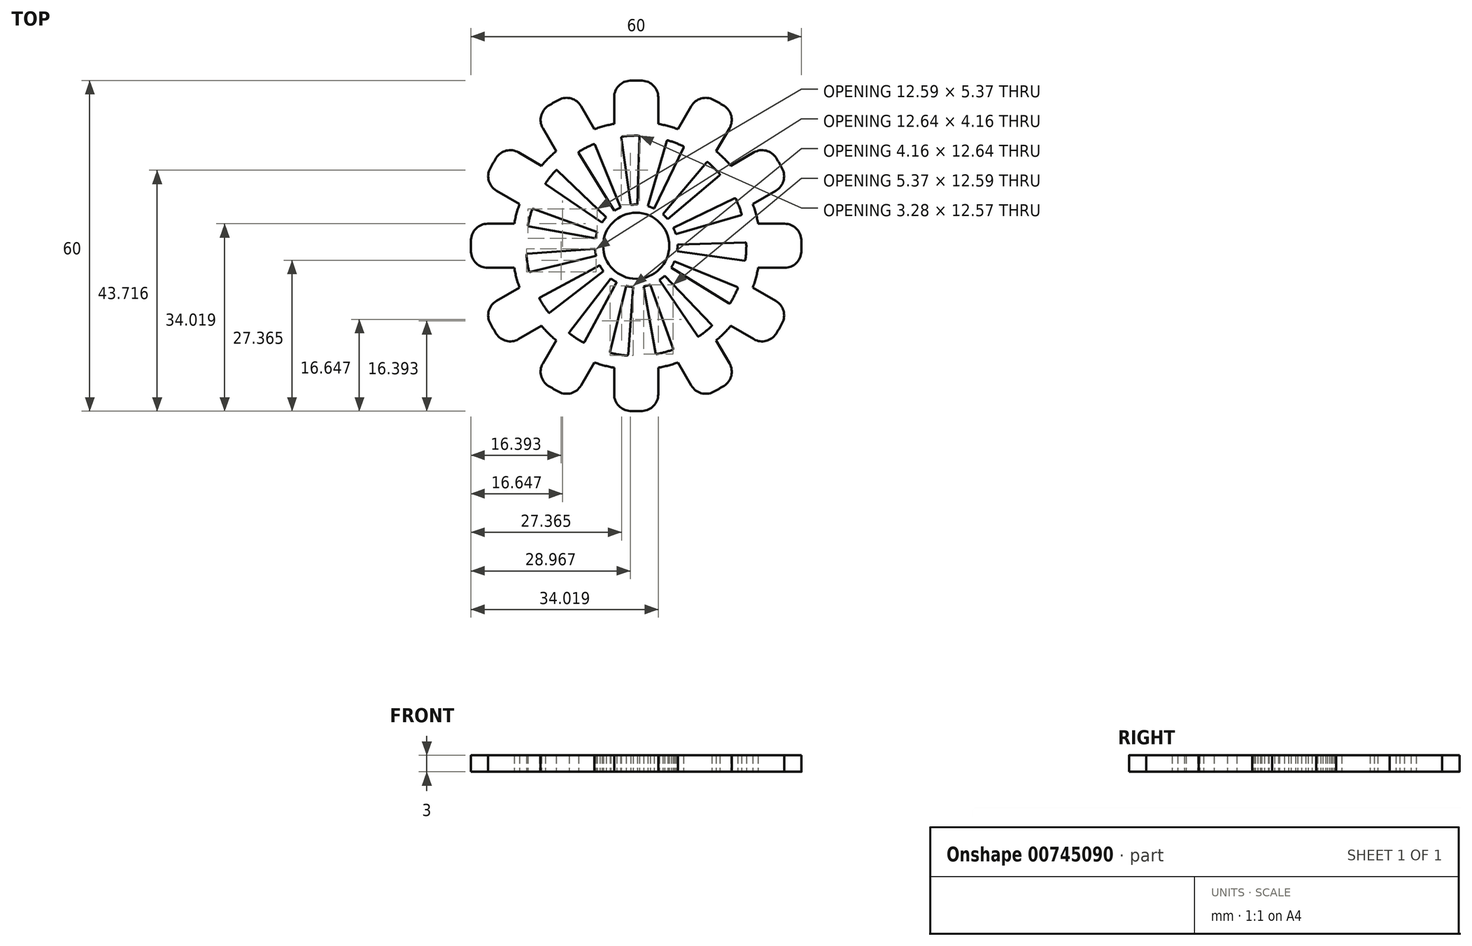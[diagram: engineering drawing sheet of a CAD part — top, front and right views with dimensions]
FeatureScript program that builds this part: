
annotation { "Feature Type Name" : "Feature", "Feature Type Description" : "" }
export const myFeature = defineFeature(function(context is Context, id is Id, definition is map)
    precondition{}
    {
        {
            var Q0;
            Q0=qCreatedBy(makeId("Top.planeOp"),FACE);
            var sketch = newSketch(context, id + "F0", { "sketchPlane" : qUnion([Q0])});
            skArc(sketch, "E0", {"start": v(-25.4, 15.95) * mm, "mid": v(-25.98, 15) * mm, "end": v(-26.52, 14.03) * mm});
            skArc(sketch, "E1", {"start": v(-7.06, 2.54) * mm, "mid": v(-7.24, 1.94) * mm, "end": v(-7.38, 1.33) * mm});
            skArc(sketch, "E2", {"start": v(-21.18, 7.6) * mm, "mid": v(-21.73, 5.82) * mm, "end": v(-22.14, 4) * mm});
            skLineSegment(sketch, "E3", {"start": v(-4, 22.14) * mm, "end": v(-4, 26.98) * mm});
            skLineSegment(sketch, "E4", {"start": v(4, 22.14) * mm, "end": v(4, 26.98) * mm});
            skLineSegment(sketch, "E5.1.0", {"start": v(-7.6, 21.18) * mm, "end": v(-10.03, 25.37) * mm});
            skLineSegment(sketch, "E5.1.1", {"start": v(-14.53, 17.18) * mm, "end": v(-16.95, 21.37) * mm});
            skLineSegment(sketch, "E5.2.0", {"start": v(-17.18, 14.53) * mm, "end": v(-21.37, 16.95) * mm});
            skLineSegment(sketch, "E5.2.1", {"start": v(-21.18, 7.6) * mm, "end": v(-25.37, 10.03) * mm});
            skLineSegment(sketch, "E5.3.0", {"start": v(-22.14, 4) * mm, "end": v(-26.98, 4) * mm});
            skLineSegment(sketch, "E5.3.1", {"start": v(-22.14, -4) * mm, "end": v(-26.98, -4) * mm});
            skLineSegment(sketch, "E5.4.0", {"start": v(-21.18, -7.6) * mm, "end": v(-25.37, -10.03) * mm});
            skLineSegment(sketch, "E5.4.1", {"start": v(-17.18, -14.53) * mm, "end": v(-21.37, -16.95) * mm});
            skLineSegment(sketch, "E5.5.0", {"start": v(-14.53, -17.18) * mm, "end": v(-16.95, -21.37) * mm});
            skLineSegment(sketch, "E5.5.1", {"start": v(-7.6, -21.18) * mm, "end": v(-10.03, -25.37) * mm});
            skLineSegment(sketch, "E5.6.0", {"start": v(-4, -22.14) * mm, "end": v(-4, -26.98) * mm});
            skLineSegment(sketch, "E5.6.1", {"start": v(4, -22.14) * mm, "end": v(4, -26.98) * mm});
            skLineSegment(sketch, "E5.7.0", {"start": v(7.6, -21.18) * mm, "end": v(10.03, -25.37) * mm});
            skLineSegment(sketch, "E5.7.1", {"start": v(14.53, -17.18) * mm, "end": v(16.95, -21.37) * mm});
            skLineSegment(sketch, "E5.8.0", {"start": v(17.18, -14.53) * mm, "end": v(21.37, -16.95) * mm});
            skLineSegment(sketch, "E5.8.1", {"start": v(21.18, -7.6) * mm, "end": v(25.37, -10.03) * mm});
            skLineSegment(sketch, "E5.9.0", {"start": v(22.14, -4) * mm, "end": v(26.98, -4) * mm});
            skLineSegment(sketch, "E5.9.1", {"start": v(22.14, 4) * mm, "end": v(26.98, 4) * mm});
            skLineSegment(sketch, "E5.10.0", {"start": v(21.18, 7.6) * mm, "end": v(25.37, 10.03) * mm});
            skLineSegment(sketch, "E5.10.1", {"start": v(17.18, 14.53) * mm, "end": v(21.37, 16.95) * mm});
            skLineSegment(sketch, "E5.11.0", {"start": v(14.53, 17.18) * mm, "end": v(16.95, 21.37) * mm});
            skLineSegment(sketch, "E5.11.1", {"start": v(7.6, 21.18) * mm, "end": v(10.03, 25.37) * mm});
            skArc(sketch, "E6.trimOffspring", {"start": v(-14.03, 26.52) * mm, "mid": v(-15, 25.98) * mm, "end": v(-15.95, 25.4) * mm});
            skArc(sketch, "E7.trimOffspring", {"start": v(1.11, 29.98) * mm, "mid": v(0, 30) * mm, "end": v(-1.11, 29.98) * mm});
            skArc(sketch, "E8.trimOffspring", {"start": v(15.95, 25.4) * mm, "mid": v(15, 25.98) * mm, "end": v(14.03, 26.52) * mm});
            skArc(sketch, "E9.trimOffspring", {"start": v(26.52, 14.03) * mm, "mid": v(25.98, 15) * mm, "end": v(25.4, 15.95) * mm});
            skArc(sketch, "E10.trimOffspring", {"start": v(29.98, -1.11) * mm, "mid": v(30, 0) * mm, "end": v(29.98, 1.11) * mm});
            skArc(sketch, "E11.trimOffspring", {"start": v(25.4, -15.95) * mm, "mid": v(25.98, -15) * mm, "end": v(26.52, -14.03) * mm});
            skArc(sketch, "E12.trimOffspring", {"start": v(14.03, -26.52) * mm, "mid": v(15, -25.98) * mm, "end": v(15.95, -25.4) * mm});
            skArc(sketch, "E13.trimOffspring", {"start": v(-1.11, -29.98) * mm, "mid": v(0, -30) * mm, "end": v(1.11, -29.98) * mm});
            skArc(sketch, "E14.trimOffspring", {"start": v(-15.95, -25.4) * mm, "mid": v(-15, -25.98) * mm, "end": v(-14.03, -26.52) * mm});
            skArc(sketch, "E15.trimOffspring", {"start": v(-26.52, -14.03) * mm, "mid": v(-25.98, -15) * mm, "end": v(-25.4, -15.95) * mm});
            skArc(sketch, "E16.trimOffspring", {"start": v(-29.98, 1.11) * mm, "mid": v(-30, 0) * mm, "end": v(-29.98, -1.11) * mm});
            skArc(sketch, "E17.trimOffspring", {"start": v(-14.53, 17.18) * mm, "mid": v(-15.9, 15.9) * mm, "end": v(-17.18, 14.53) * mm});
            skArc(sketch, "E18.trimOffspring", {"start": v(-4, 22.14) * mm, "mid": v(-5.82, 21.73) * mm, "end": v(-7.6, 21.18) * mm});
            skArc(sketch, "E19.trimOffspring", {"start": v(7.6, 21.18) * mm, "mid": v(5.82, 21.73) * mm, "end": v(4, 22.14) * mm});
            skArc(sketch, "E20.trimOffspring", {"start": v(17.18, 14.53) * mm, "mid": v(15.9, 15.9) * mm, "end": v(14.53, 17.18) * mm});
            skArc(sketch, "E21.trimOffspring", {"start": v(22.14, 4) * mm, "mid": v(21.73, 5.82) * mm, "end": v(21.18, 7.6) * mm});
            skArc(sketch, "E22.trimOffspring", {"start": v(21.18, -7.6) * mm, "mid": v(21.73, -5.82) * mm, "end": v(22.14, -4) * mm});
            skArc(sketch, "E23.trimOffspring", {"start": v(14.53, -17.18) * mm, "mid": v(15.9, -15.9) * mm, "end": v(17.18, -14.53) * mm});
            skArc(sketch, "E24.trimOffspring", {"start": v(4, -22.14) * mm, "mid": v(5.82, -21.73) * mm, "end": v(7.6, -21.18) * mm});
            skArc(sketch, "E25.trimOffspring", {"start": v(-7.6, -21.18) * mm, "mid": v(-5.82, -21.73) * mm, "end": v(-4, -22.14) * mm});
            skArc(sketch, "E26.trimOffspring", {"start": v(-17.18, -14.53) * mm, "mid": v(-15.9, -15.9) * mm, "end": v(-14.53, -17.18) * mm});
            skArc(sketch, "E27.trimOffspring", {"start": v(-22.14, -4) * mm, "mid": v(-21.73, -5.82) * mm, "end": v(-21.18, -7.6) * mm});
            skPoint(sketch, "E28.visualSharp", {"position": v(-18.33, 23.75) * mm});
            skArc(sketch, "E28.filletArc", {"start": v(-15.95, 25.4) * mm, "mid": v(-17.27, 23.59) * mm, "end": v(-16.95, 21.37) * mm});
            skPoint(sketch, "E29.visualSharp", {"position": v(-11.4, 27.75) * mm});
            skArc(sketch, "E29.filletArc", {"start": v(-10.03, 25.37) * mm, "mid": v(-11.8, 26.75) * mm, "end": v(-14.03, 26.52) * mm});
            skPoint(sketch, "E30.visualSharp", {"position": v(-4, 29.73) * mm});
            skArc(sketch, "E30.filletArc", {"start": v(-1.11, 29.98) * mm, "mid": v(-3.16, 29.06) * mm, "end": v(-4, 26.98) * mm});
            skPoint(sketch, "E31.visualSharp", {"position": v(4, 29.73) * mm});
            skArc(sketch, "E31.filletArc", {"start": v(4, 26.98) * mm, "mid": v(3.16, 29.06) * mm, "end": v(1.11, 29.98) * mm});
            skPoint(sketch, "E32.visualSharp", {"position": v(11.4, 27.75) * mm});
            skArc(sketch, "E32.filletArc", {"start": v(14.03, 26.52) * mm, "mid": v(11.8, 26.75) * mm, "end": v(10.03, 25.37) * mm});
            skPoint(sketch, "E33.visualSharp", {"position": v(18.33, 23.75) * mm});
            skArc(sketch, "E33.filletArc", {"start": v(16.95, 21.37) * mm, "mid": v(17.27, 23.59) * mm, "end": v(15.95, 25.4) * mm});
            skPoint(sketch, "E34.visualSharp", {"position": v(23.75, 18.33) * mm});
            skArc(sketch, "E34.filletArc", {"start": v(25.4, 15.95) * mm, "mid": v(23.59, 17.27) * mm, "end": v(21.37, 16.95) * mm});
            skPoint(sketch, "E35.visualSharp", {"position": v(27.75, 11.4) * mm});
            skArc(sketch, "E35.filletArc", {"start": v(25.37, 10.03) * mm, "mid": v(26.75, 11.8) * mm, "end": v(26.52, 14.03) * mm});
            skPoint(sketch, "E36.visualSharp", {"position": v(29.73, 4) * mm});
            skArc(sketch, "E36.filletArc", {"start": v(29.98, 1.11) * mm, "mid": v(29.06, 3.16) * mm, "end": v(26.98, 4) * mm});
            skPoint(sketch, "E37.visualSharp", {"position": v(29.73, -4) * mm});
            skArc(sketch, "E37.filletArc", {"start": v(26.98, -4) * mm, "mid": v(29.06, -3.16) * mm, "end": v(29.98, -1.11) * mm});
            skPoint(sketch, "E38.visualSharp", {"position": v(27.75, -11.4) * mm});
            skArc(sketch, "E38.filletArc", {"start": v(26.52, -14.03) * mm, "mid": v(26.75, -11.8) * mm, "end": v(25.37, -10.03) * mm});
            skPoint(sketch, "E39.visualSharp", {"position": v(23.75, -18.33) * mm});
            skArc(sketch, "E39.filletArc", {"start": v(21.37, -16.95) * mm, "mid": v(23.59, -17.27) * mm, "end": v(25.4, -15.95) * mm});
            skPoint(sketch, "E40.visualSharp", {"position": v(18.33, -23.75) * mm});
            skArc(sketch, "E40.filletArc", {"start": v(15.95, -25.4) * mm, "mid": v(17.27, -23.59) * mm, "end": v(16.95, -21.37) * mm});
            skPoint(sketch, "E41.visualSharp", {"position": v(11.4, -27.75) * mm});
            skArc(sketch, "E41.filletArc", {"start": v(10.03, -25.37) * mm, "mid": v(11.8, -26.75) * mm, "end": v(14.03, -26.52) * mm});
            skPoint(sketch, "E42.visualSharp", {"position": v(4, -29.73) * mm});
            skArc(sketch, "E42.filletArc", {"start": v(1.11, -29.98) * mm, "mid": v(3.16, -29.06) * mm, "end": v(4, -26.98) * mm});
            skPoint(sketch, "E43.visualSharp", {"position": v(-4, -29.73) * mm});
            skArc(sketch, "E43.filletArc", {"start": v(-4, -26.98) * mm, "mid": v(-3.16, -29.06) * mm, "end": v(-1.11, -29.98) * mm});
            skPoint(sketch, "E44.visualSharp", {"position": v(-11.4, -27.75) * mm});
            skArc(sketch, "E44.filletArc", {"start": v(-14.03, -26.52) * mm, "mid": v(-11.8, -26.75) * mm, "end": v(-10.03, -25.37) * mm});
            skPoint(sketch, "E45.visualSharp", {"position": v(-18.33, -23.75) * mm});
            skArc(sketch, "E45.filletArc", {"start": v(-16.95, -21.37) * mm, "mid": v(-17.27, -23.59) * mm, "end": v(-15.95, -25.4) * mm});
            skPoint(sketch, "E46.visualSharp", {"position": v(-23.75, -18.33) * mm});
            skArc(sketch, "E46.filletArc", {"start": v(-25.4, -15.95) * mm, "mid": v(-23.59, -17.27) * mm, "end": v(-21.37, -16.95) * mm});
            skPoint(sketch, "E47.visualSharp", {"position": v(-27.75, -11.4) * mm});
            skArc(sketch, "E47.filletArc", {"start": v(-25.37, -10.03) * mm, "mid": v(-26.75, -11.8) * mm, "end": v(-26.52, -14.03) * mm});
            skPoint(sketch, "E48.visualSharp", {"position": v(-29.73, -4) * mm});
            skArc(sketch, "E48.filletArc", {"start": v(-29.98, -1.11) * mm, "mid": v(-29.06, -3.16) * mm, "end": v(-26.98, -4) * mm});
            skPoint(sketch, "E49.visualSharp", {"position": v(-29.73, 4) * mm});
            skArc(sketch, "E49.filletArc", {"start": v(-26.98, 4) * mm, "mid": v(-29.06, 3.16) * mm, "end": v(-29.98, 1.11) * mm});
            skPoint(sketch, "E50.visualSharp", {"position": v(-27.75, 11.4) * mm});
            skArc(sketch, "E50.filletArc", {"start": v(-26.52, 14.03) * mm, "mid": v(-26.75, 11.8) * mm, "end": v(-25.37, 10.03) * mm});
            skPoint(sketch, "E51.visualSharp", {"position": v(-23.75, 18.33) * mm});
            skArc(sketch, "E51.filletArc", {"start": v(-21.37, 16.95) * mm, "mid": v(-23.59, 17.27) * mm, "end": v(-25.4, 15.95) * mm});
            skLineSegment(sketch, "E52", {"start": v(-18.63, 6.7) * mm, "end": v(-7.06, 2.54) * mm});
            skLineSegment(sketch, "E53", {"start": v(-7.38, 1.33) * mm, "end": v(-19.48, 3.52) * mm});
            skArc(sketch, "E54", {"start": v(-18.89, 6.57) * mm, "mid": v(-19.32, 5.18) * mm, "end": v(-19.64, 3.75) * mm});
            skPoint(sketch, "E55.visualSharp", {"position": v(-18.82, 6.76) * mm});
            skArc(sketch, "E55.filletArc", {"start": v(-18.63, 6.7) * mm, "mid": v(-18.79, 6.69) * mm, "end": v(-18.89, 6.57) * mm});
            skPoint(sketch, "E56.visualSharp", {"position": v(-19.68, 3.56) * mm});
            skArc(sketch, "E56.filletArc", {"start": v(-19.64, 3.75) * mm, "mid": v(-19.61, 3.6) * mm, "end": v(-19.48, 3.52) * mm});
            skCircle(sketch, "E57", {"center": v(0, 0) * mm, "radius": 6 * mm});
            skLineSegment(sketch, "E58.1.0", {"start": v(-7.28, -1.78) * mm, "end": v(-19.23, -4.7) * mm});
            skArc(sketch, "E58.1.1", {"start": v(-7.48, -0.55) * mm, "mid": v(-7.4, -1.17) * mm, "end": v(-7.28, -1.78) * mm});
            skLineSegment(sketch, "E58.1.2", {"start": v(-19.74, -1.46) * mm, "end": v(-7.48, -0.55) * mm});
            skArc(sketch, "E58.1.3", {"start": v(-19.47, -4.56) * mm, "mid": v(-19.38, -4.69) * mm, "end": v(-19.23, -4.7) * mm});
            skPoint(sketch, "E58.1.4", {"position": v(-19.43, -4.76) * mm});
            skArc(sketch, "E58.1.5", {"start": v(-19.93, -1.68) * mm, "mid": v(-19.75, -3.13) * mm, "end": v(-19.47, -4.56) * mm});
            skPoint(sketch, "E58.1.6", {"position": v(-19.95, -1.48) * mm});
            skArc(sketch, "E58.1.7", {"start": v(-19.74, -1.46) * mm, "mid": v(-19.88, -1.53) * mm, "end": v(-19.93, -1.68) * mm});
            skLineSegment(sketch, "E58.2.0", {"start": v(-5.93, -4.6) * mm, "end": v(-15.65, -12.12) * mm});
            skArc(sketch, "E58.2.1", {"start": v(-6.6, -3.55) * mm, "mid": v(-6.3, -4.08) * mm, "end": v(-5.93, -4.6) * mm});
            skLineSegment(sketch, "E58.2.2", {"start": v(-17.44, -9.37) * mm, "end": v(-6.6, -3.55) * mm});
            skArc(sketch, "E58.2.3", {"start": v(-15.93, -12.09) * mm, "mid": v(-15.8, -12.16) * mm, "end": v(-15.65, -12.12) * mm});
            skPoint(sketch, "E58.2.4", {"position": v(-15.81, -12.25) * mm});
            skArc(sketch, "E58.2.5", {"start": v(-17.52, -9.64) * mm, "mid": v(-16.77, -10.9) * mm, "end": v(-15.93, -12.09) * mm});
            skPoint(sketch, "E58.2.6", {"position": v(-17.62, -9.46) * mm});
            skArc(sketch, "E58.2.7", {"start": v(-17.44, -9.37) * mm, "mid": v(-17.54, -9.49) * mm, "end": v(-17.52, -9.64) * mm});
            skLineSegment(sketch, "E58.3.0", {"start": v(-3.55, -6.6) * mm, "end": v(-9.37, -17.44) * mm});
            skArc(sketch, "E58.3.1", {"start": v(-4.6, -5.93) * mm, "mid": v(-4.08, -6.3) * mm, "end": v(-3.55, -6.6) * mm});
            skLineSegment(sketch, "E58.3.2", {"start": v(-12.12, -15.65) * mm, "end": v(-4.6, -5.93) * mm});
            skArc(sketch, "E58.3.3", {"start": v(-9.64, -17.52) * mm, "mid": v(-9.49, -17.54) * mm, "end": v(-9.37, -17.44) * mm});
            skPoint(sketch, "E58.3.4", {"position": v(-9.46, -17.62) * mm});
            skArc(sketch, "E58.3.5", {"start": v(-12.09, -15.93) * mm, "mid": v(-10.9, -16.77) * mm, "end": v(-9.64, -17.52) * mm});
            skPoint(sketch, "E58.3.6", {"position": v(-12.25, -15.81) * mm});
            skArc(sketch, "E58.3.7", {"start": v(-12.12, -15.65) * mm, "mid": v(-12.16, -15.8) * mm, "end": v(-12.09, -15.93) * mm});
            skLineSegment(sketch, "E58.4.0", {"start": v(-0.55, -7.48) * mm, "end": v(-1.46, -19.74) * mm});
            skArc(sketch, "E58.4.1", {"start": v(-1.78, -7.28) * mm, "mid": v(-1.17, -7.4) * mm, "end": v(-0.55, -7.48) * mm});
            skLineSegment(sketch, "E58.4.2", {"start": v(-4.7, -19.23) * mm, "end": v(-1.78, -7.28) * mm});
            skArc(sketch, "E58.4.3", {"start": v(-1.68, -19.93) * mm, "mid": v(-1.53, -19.88) * mm, "end": v(-1.46, -19.74) * mm});
            skPoint(sketch, "E58.4.4", {"position": v(-1.48, -19.95) * mm});
            skArc(sketch, "E58.4.5", {"start": v(-4.56, -19.47) * mm, "mid": v(-3.13, -19.75) * mm, "end": v(-1.68, -19.93) * mm});
            skPoint(sketch, "E58.4.6", {"position": v(-4.76, -19.43) * mm});
            skArc(sketch, "E58.4.7", {"start": v(-4.7, -19.23) * mm, "mid": v(-4.69, -19.38) * mm, "end": v(-4.56, -19.47) * mm});
            skLineSegment(sketch, "E58.5.0", {"start": v(2.54, -7.06) * mm, "end": v(6.7, -18.63) * mm});
            skArc(sketch, "E58.5.1", {"start": v(1.33, -7.38) * mm, "mid": v(1.94, -7.24) * mm, "end": v(2.54, -7.06) * mm});
            skLineSegment(sketch, "E58.5.2", {"start": v(3.52, -19.48) * mm, "end": v(1.33, -7.38) * mm});
            skArc(sketch, "E58.5.3", {"start": v(6.57, -18.89) * mm, "mid": v(6.69, -18.79) * mm, "end": v(6.7, -18.63) * mm});
            skPoint(sketch, "E58.5.4", {"position": v(6.76, -18.82) * mm});
            skArc(sketch, "E58.5.5", {"start": v(3.75, -19.64) * mm, "mid": v(5.18, -19.32) * mm, "end": v(6.57, -18.89) * mm});
            skPoint(sketch, "E58.5.6", {"position": v(3.56, -19.68) * mm});
            skArc(sketch, "E58.5.7", {"start": v(3.52, -19.48) * mm, "mid": v(3.6, -19.61) * mm, "end": v(3.75, -19.64) * mm});
            skLineSegment(sketch, "E58.6.0", {"start": v(13.7, -14.3) * mm, "end": v(5.19, -5.42) * mm});
            skArc(sketch, "E58.6.1", {"start": v(4.22, -6.2) * mm, "mid": v(4.72, -5.83) * mm, "end": v(5.19, -5.42) * mm});
            skLineSegment(sketch, "E58.6.2", {"start": v(11.14, -16.37) * mm, "end": v(4.22, -6.2) * mm});
            skArc(sketch, "E58.6.3", {"start": v(13.69, -14.58) * mm, "mid": v(13.75, -14.44) * mm, "end": v(13.7, -14.3) * mm});
            skPoint(sketch, "E58.6.4", {"position": v(13.83, -14.44) * mm});
            skArc(sketch, "E58.6.5", {"start": v(11.42, -16.42) * mm, "mid": v(12.59, -15.54) * mm, "end": v(13.69, -14.58) * mm});
            skPoint(sketch, "E58.6.6", {"position": v(11.25, -16.53) * mm});
            skArc(sketch, "E58.6.7", {"start": v(11.14, -16.37) * mm, "mid": v(11.27, -16.45) * mm, "end": v(11.42, -16.42) * mm});
            skLineSegment(sketch, "E58.7.0", {"start": v(6.94, -2.84) * mm, "end": v(18.33, -7.5) * mm});
            skArc(sketch, "E58.7.1", {"start": v(6.38, -3.95) * mm, "mid": v(6.68, -3.4) * mm, "end": v(6.94, -2.84) * mm});
            skLineSegment(sketch, "E58.7.2", {"start": v(16.83, -10.42) * mm, "end": v(6.38, -3.95) * mm});
            skArc(sketch, "E58.7.3", {"start": v(18.43, -7.76) * mm, "mid": v(18.44, -7.6) * mm, "end": v(18.33, -7.5) * mm});
            skPoint(sketch, "E58.7.4", {"position": v(18.51, -7.57) * mm});
            skArc(sketch, "E58.7.5", {"start": v(17.11, -10.35) * mm, "mid": v(17.82, -9.08) * mm, "end": v(18.43, -7.76) * mm});
            skPoint(sketch, "E58.7.6", {"position": v(17, -10.53) * mm});
            skArc(sketch, "E58.7.7", {"start": v(16.83, -10.42) * mm, "mid": v(16.99, -10.45) * mm, "end": v(17.11, -10.35) * mm});
            skLineSegment(sketch, "E58.8.0", {"start": v(7.5, 0.23) * mm, "end": v(19.79, 0.6) * mm});
            skArc(sketch, "E58.8.1", {"start": v(7.43, -1.01) * mm, "mid": v(7.49, -0.4) * mm, "end": v(7.5, 0.23) * mm});
            skLineSegment(sketch, "E58.8.2", {"start": v(19.62, -2.67) * mm, "end": v(7.43, -1.01) * mm});
            skArc(sketch, "E58.8.3", {"start": v(20, 0.41) * mm, "mid": v(19.93, 0.55) * mm, "end": v(19.79, 0.6) * mm});
            skPoint(sketch, "E58.8.4", {"position": v(20, 0.61) * mm});
            skArc(sketch, "E58.8.5", {"start": v(19.84, -2.5) * mm, "mid": v(19.97, -1.05) * mm, "end": v(20, 0.41) * mm});
            skPoint(sketch, "E58.8.6", {"position": v(19.82, -2.7) * mm});
            skArc(sketch, "E58.8.7", {"start": v(19.62, -2.67) * mm, "mid": v(19.77, -2.63) * mm, "end": v(19.84, -2.5) * mm});
            skLineSegment(sketch, "E58.9.0", {"start": v(6.75, 3.26) * mm, "end": v(17.83, 8.6) * mm});
            skArc(sketch, "E58.9.1", {"start": v(7.2, 2.1) * mm, "mid": v(7, 2.69) * mm, "end": v(6.75, 3.26) * mm});
            skLineSegment(sketch, "E58.9.2", {"start": v(19, 5.54) * mm, "end": v(7.2, 2.1) * mm});
            skArc(sketch, "E58.9.3", {"start": v(18.1, 8.5) * mm, "mid": v(17.99, 8.61) * mm, "end": v(17.83, 8.6) * mm});
            skPoint(sketch, "E58.9.4", {"position": v(18.01, 8.7) * mm});
            skArc(sketch, "E58.9.5", {"start": v(19.14, 5.79) * mm, "mid": v(18.67, 7.17) * mm, "end": v(18.1, 8.5) * mm});
            skPoint(sketch, "E58.9.6", {"position": v(19.2, 5.6) * mm});
            skArc(sketch, "E58.9.7", {"start": v(19, 5.54) * mm, "mid": v(19.13, 5.63) * mm, "end": v(19.14, 5.79) * mm});
            skLineSegment(sketch, "E58.10.0", {"start": v(4.84, 5.73) * mm, "end": v(12.8, 15.11) * mm});
            skArc(sketch, "E58.10.1", {"start": v(5.73, 4.84) * mm, "mid": v(5.3, 5.3) * mm, "end": v(4.84, 5.73) * mm});
            skLineSegment(sketch, "E58.10.2", {"start": v(15.11, 12.8) * mm, "end": v(5.73, 4.84) * mm});
            skArc(sketch, "E58.10.3", {"start": v(13.07, 15.14) * mm, "mid": v(12.93, 15.18) * mm, "end": v(12.8, 15.11) * mm});
            skPoint(sketch, "E58.10.4", {"position": v(12.92, 15.27) * mm});
            skArc(sketch, "E58.10.5", {"start": v(15.14, 13.07) * mm, "mid": v(14.14, 14.14) * mm, "end": v(13.07, 15.14) * mm});
            skPoint(sketch, "E58.10.6", {"position": v(15.27, 12.92) * mm});
            skArc(sketch, "E58.10.7", {"start": v(15.11, 12.8) * mm, "mid": v(15.18, 12.93) * mm, "end": v(15.14, 13.07) * mm});
            skLineSegment(sketch, "E58.11.0", {"start": v(2.1, 7.2) * mm, "end": v(5.54, 19) * mm});
            skArc(sketch, "E58.11.1", {"start": v(3.26, 6.75) * mm, "mid": v(2.69, 7) * mm, "end": v(2.1, 7.2) * mm});
            skLineSegment(sketch, "E58.11.2", {"start": v(8.6, 17.83) * mm, "end": v(3.26, 6.75) * mm});
            skArc(sketch, "E58.11.3", {"start": v(5.79, 19.14) * mm, "mid": v(5.63, 19.13) * mm, "end": v(5.54, 19) * mm});
            skPoint(sketch, "E58.11.4", {"position": v(5.6, 19.2) * mm});
            skArc(sketch, "E58.11.5", {"start": v(8.5, 18.1) * mm, "mid": v(7.17, 18.67) * mm, "end": v(5.79, 19.14) * mm});
            skPoint(sketch, "E58.11.6", {"position": v(8.7, 18.01) * mm});
            skArc(sketch, "E58.11.7", {"start": v(8.6, 17.83) * mm, "mid": v(8.61, 17.99) * mm, "end": v(8.5, 18.1) * mm});
            skLineSegment(sketch, "E58.12.0", {"start": v(-1.01, 7.43) * mm, "end": v(-2.67, 19.62) * mm});
            skArc(sketch, "E58.12.1", {"start": v(0.23, 7.5) * mm, "mid": v(-0.4, 7.49) * mm, "end": v(-1.01, 7.43) * mm});
            skLineSegment(sketch, "E58.12.2", {"start": v(0.6, 19.79) * mm, "end": v(0.23, 7.5) * mm});
            skArc(sketch, "E58.12.3", {"start": v(-2.5, 19.84) * mm, "mid": v(-2.63, 19.77) * mm, "end": v(-2.67, 19.62) * mm});
            skPoint(sketch, "E58.12.4", {"position": v(-2.7, 19.82) * mm});
            skArc(sketch, "E58.12.5", {"start": v(0.41, 20) * mm, "mid": v(-1.05, 19.97) * mm, "end": v(-2.5, 19.84) * mm});
            skPoint(sketch, "E58.12.6", {"position": v(0.61, 20) * mm});
            skArc(sketch, "E58.12.7", {"start": v(0.6, 19.79) * mm, "mid": v(0.55, 19.93) * mm, "end": v(0.41, 20) * mm});
            skLineSegment(sketch, "E58.13.0", {"start": v(-3.95, 6.38) * mm, "end": v(-10.42, 16.83) * mm});
            skArc(sketch, "E58.13.1", {"start": v(-2.84, 6.94) * mm, "mid": v(-3.4, 6.68) * mm, "end": v(-3.95, 6.38) * mm});
            skLineSegment(sketch, "E58.13.2", {"start": v(-7.5, 18.33) * mm, "end": v(-2.84, 6.94) * mm});
            skArc(sketch, "E58.13.3", {"start": v(-10.35, 17.11) * mm, "mid": v(-10.45, 16.99) * mm, "end": v(-10.42, 16.83) * mm});
            skPoint(sketch, "E58.13.4", {"position": v(-10.53, 17) * mm});
            skArc(sketch, "E58.13.5", {"start": v(-7.76, 18.43) * mm, "mid": v(-9.08, 17.82) * mm, "end": v(-10.35, 17.11) * mm});
            skPoint(sketch, "E58.13.6", {"position": v(-7.57, 18.51) * mm});
            skArc(sketch, "E58.13.7", {"start": v(-7.5, 18.33) * mm, "mid": v(-7.6, 18.44) * mm, "end": v(-7.76, 18.43) * mm});
            skLineSegment(sketch, "E58.14.0", {"start": v(-6.2, 4.22) * mm, "end": v(-16.37, 11.14) * mm});
            skArc(sketch, "E58.14.1", {"start": v(-5.42, 5.19) * mm, "mid": v(-5.83, 4.72) * mm, "end": v(-6.2, 4.22) * mm});
            skLineSegment(sketch, "E58.14.2", {"start": v(-14.3, 13.7) * mm, "end": v(-5.42, 5.19) * mm});
            skArc(sketch, "E58.14.3", {"start": v(-16.42, 11.42) * mm, "mid": v(-16.45, 11.27) * mm, "end": v(-16.37, 11.14) * mm});
            skPoint(sketch, "E58.14.4", {"position": v(-16.53, 11.25) * mm});
            skArc(sketch, "E58.14.5", {"start": v(-14.58, 13.69) * mm, "mid": v(-15.54, 12.59) * mm, "end": v(-16.42, 11.42) * mm});
            skPoint(sketch, "E58.14.6", {"position": v(-14.44, 13.83) * mm});
            skArc(sketch, "E58.14.7", {"start": v(-14.3, 13.7) * mm, "mid": v(-14.44, 13.75) * mm, "end": v(-14.58, 13.69) * mm});
            skSolve(sketch);
        }
        {
            var Q0;
            Q0=makeQuery(id+"F0.imprint","IMPRINT",FACE,{"disambiguationData":[TD([[makeQuery(id+"F0.imprint","IMPRINT",EDGE,{"derivedFrom":sQuery(id+"F0.wireOp",EDGE,"E0")}),1.0]])]});
            extrude(context, id + "F1", {"entities" : qUnion([Q0]), "depth" : 3 * mm, "offsetDistance" : 25 * mm});
        }
    });
